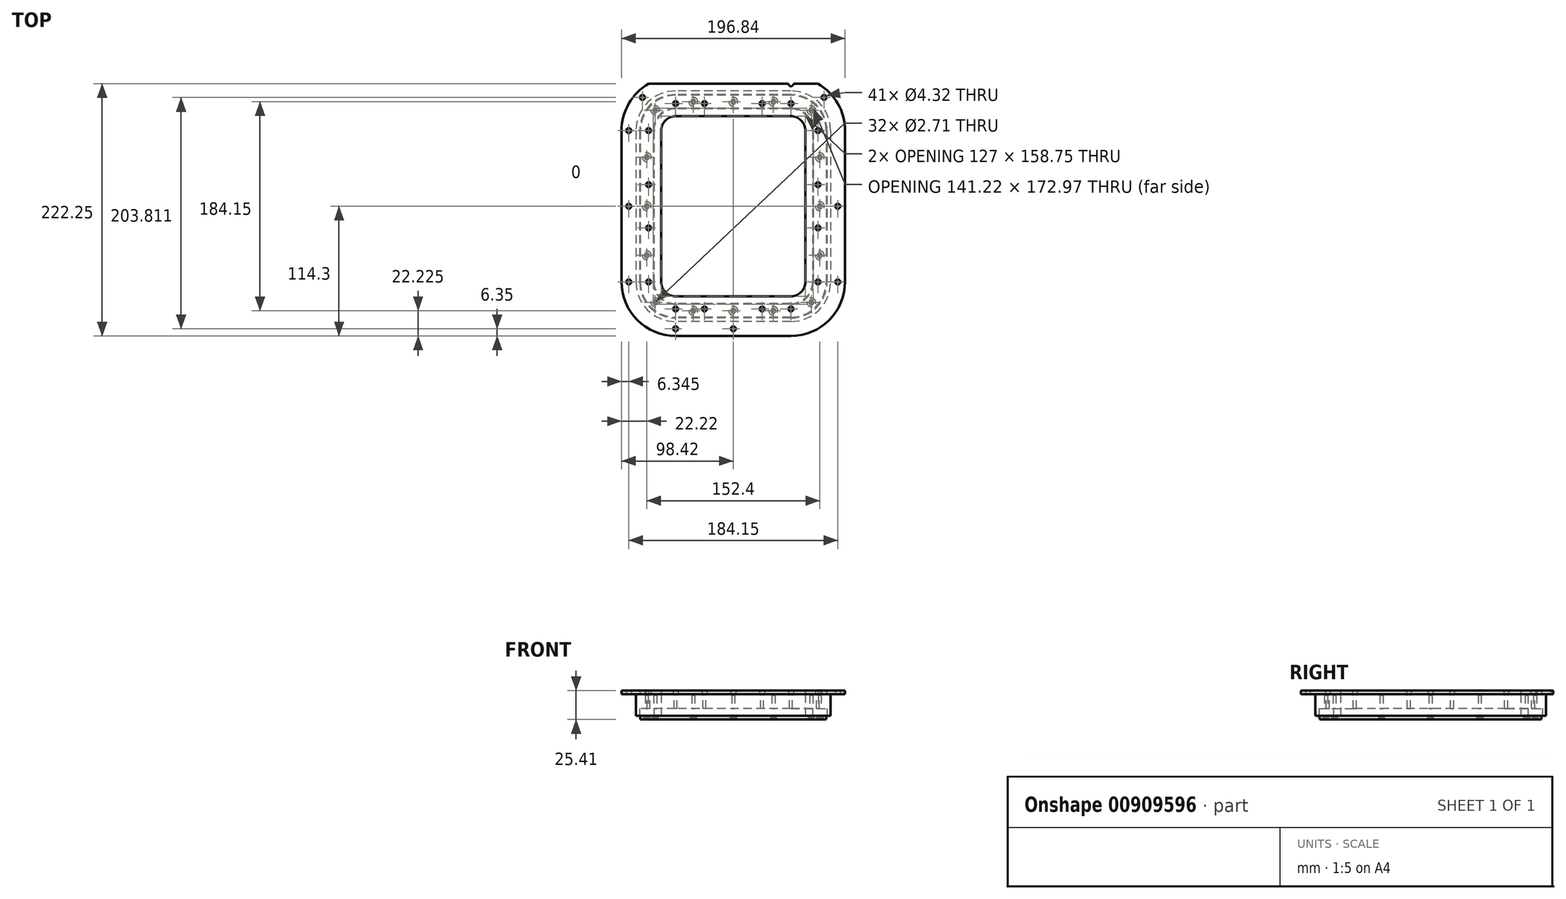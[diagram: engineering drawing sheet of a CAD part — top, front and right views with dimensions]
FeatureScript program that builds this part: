
annotation { "Feature Type Name" : "Feature", "Feature Type Description" : "" }
export const myFeature = defineFeature(function(context is Context, id is Id, definition is map)
    precondition{}
    {
        {
            var Q0;
            Q0=qCreatedBy(makeId("Top.planeOp"),FACE);
            var sketch = newSketch(context, id + "F0", { "sketchPlane" : qUnion([Q0])});
            skLineSegment(sketch, "E0.bottom", {"start": v(50.8, 79.38) * mm, "end": v(-50.8, 79.38) * mm});
            skLineSegment(sketch, "E0.top", {"start": v(50.8, -79.38) * mm, "end": v(-50.8, -79.38) * mm});
            skLineSegment(sketch, "E0.left", {"start": v(63.5, 66.67) * mm, "end": v(63.5, -66.67) * mm});
            skLineSegment(sketch, "E0.right", {"start": v(-63.5, 66.67) * mm, "end": v(-63.5, -66.67) * mm});
            skPoint(sketch, "E0.middle", {"position": v(0, 0) * mm});
            skPoint(sketch, "E1.visualSharp", {"position": v(-63.5, 79.38) * mm});
            skArc(sketch, "E1.filletArc", {"start": v(-50.8, 79.38) * mm, "mid": v(-59.78, 75.66) * mm, "end": v(-63.5, 66.67) * mm});
            skPoint(sketch, "E2.visualSharp", {"position": v(63.5, 79.38) * mm});
            skArc(sketch, "E2.filletArc", {"start": v(63.5, 66.67) * mm, "mid": v(59.78, 75.66) * mm, "end": v(50.8, 79.38) * mm});
            skPoint(sketch, "E3.visualSharp", {"position": v(63.5, -79.38) * mm});
            skArc(sketch, "E3.filletArc", {"start": v(50.8, -79.38) * mm, "mid": v(59.78, -75.66) * mm, "end": v(63.5, -66.67) * mm});
            skPoint(sketch, "E4.visualSharp", {"position": v(-63.5, -79.38) * mm});
            skArc(sketch, "E4.filletArc", {"start": v(-63.5, -66.67) * mm, "mid": v(-59.78, -75.66) * mm, "end": v(-50.8, -79.38) * mm});
            skArc(sketch, "E5.0", {"start": v(-50.8, 85.72) * mm, "mid": v(-64.27, 80.15) * mm, "end": v(-69.85, 66.67) * mm});
            skLineSegment(sketch, "E5.1", {"start": v(50.8, 85.72) * mm, "end": v(-50.8, 85.72) * mm});
            skLineSegment(sketch, "E5.2", {"start": v(-69.85, 66.67) * mm, "end": v(-69.85, -66.67) * mm});
            skArc(sketch, "E5.3", {"start": v(69.85, 66.67) * mm, "mid": v(64.27, 80.15) * mm, "end": v(50.8, 85.72) * mm});
            skArc(sketch, "E5.4", {"start": v(-69.85, -66.67) * mm, "mid": v(-64.27, -80.15) * mm, "end": v(-50.8, -85.72) * mm});
            skLineSegment(sketch, "E5.5", {"start": v(50.8, -85.72) * mm, "end": v(-50.8, -85.72) * mm});
            skArc(sketch, "E5.6", {"start": v(50.8, -85.72) * mm, "mid": v(64.27, -80.15) * mm, "end": v(69.85, -66.67) * mm});
            skLineSegment(sketch, "E5.7", {"start": v(69.85, 66.67) * mm, "end": v(69.85, -66.67) * mm});
            skLineSegment(sketch, "E6.0", {"start": v(-70.61, 66.67) * mm, "end": v(-70.61, -66.67) * mm});
            skArc(sketch, "E6.1", {"start": v(-50.8, 86.49) * mm, "mid": v(-64.8, 80.68) * mm, "end": v(-70.61, 66.67) * mm});
            skArc(sketch, "E6.2", {"start": v(-70.61, -66.67) * mm, "mid": v(-64.8, -80.68) * mm, "end": v(-50.8, -86.49) * mm});
            skLineSegment(sketch, "E6.3", {"start": v(50.8, 86.49) * mm, "end": v(-50.8, 86.49) * mm});
            skLineSegment(sketch, "E6.4", {"start": v(50.8, -86.49) * mm, "end": v(-50.8, -86.49) * mm});
            skArc(sketch, "E6.5", {"start": v(50.8, -86.49) * mm, "mid": v(64.8, -80.68) * mm, "end": v(70.61, -66.67) * mm});
            skLineSegment(sketch, "E6.6", {"start": v(70.61, 66.67) * mm, "end": v(70.61, -66.67) * mm});
            skArc(sketch, "E6.7", {"start": v(70.61, 66.67) * mm, "mid": v(64.8, 80.68) * mm, "end": v(50.8, 86.49) * mm});
            skArc(sketch, "E7.0", {"start": v(50.8, -98.42) * mm, "mid": v(73.25, -89.13) * mm, "end": v(82.55, -66.67) * mm});
            skLineSegment(sketch, "E7.1", {"start": v(82.55, 66.67) * mm, "end": v(82.55, -66.67) * mm});
            skLineSegment(sketch, "E7.2", {"start": v(50.8, -98.42) * mm, "end": v(-50.8, -98.42) * mm});
            skArc(sketch, "E7.3", {"start": v(82.55, 66.67) * mm, "mid": v(73.25, 89.13) * mm, "end": v(50.8, 98.42) * mm});
            skArc(sketch, "E7.4", {"start": v(-82.55, -66.67) * mm, "mid": v(-73.25, -89.13) * mm, "end": v(-50.8, -98.42) * mm});
            skLineSegment(sketch, "E7.5", {"start": v(-82.55, 66.67) * mm, "end": v(-82.55, -66.67) * mm});
            skArc(sketch, "E7.6", {"start": v(-50.8, 98.42) * mm, "mid": v(-73.25, 89.13) * mm, "end": v(-82.55, 66.67) * mm});
            skLineSegment(sketch, "E7.7", {"start": v(50.8, 98.42) * mm, "end": v(-50.8, 98.42) * mm});
            skArc(sketch, "E8.0", {"start": v(50.8, -101.6) * mm, "mid": v(75.5, -91.37) * mm, "end": v(85.72, -66.67) * mm});
            skLineSegment(sketch, "E8.1", {"start": v(85.73, 66.67) * mm, "end": v(85.73, -66.67) * mm});
            skLineSegment(sketch, "E8.2", {"start": v(50.8, -101.6) * mm, "end": v(-50.8, -101.6) * mm});
            skArc(sketch, "E8.3", {"start": v(85.73, 66.67) * mm, "mid": v(75.5, 91.37) * mm, "end": v(50.8, 101.6) * mm});
            skArc(sketch, "E8.4", {"start": v(-85.72, -66.67) * mm, "mid": v(-75.5, -91.37) * mm, "end": v(-50.8, -101.6) * mm});
            skLineSegment(sketch, "E8.5", {"start": v(-85.72, 66.67) * mm, "end": v(-85.72, -66.67) * mm});
            skArc(sketch, "E8.6", {"start": v(-50.8, 101.6) * mm, "mid": v(-75.5, 91.37) * mm, "end": v(-85.72, 66.67) * mm});
            skLineSegment(sketch, "E8.7", {"start": v(50.8, 101.6) * mm, "end": v(-50.8, 101.6) * mm});
            skArc(sketch, "E9.0", {"start": v(50.8, -97.66) * mm, "mid": v(72.71, -88.59) * mm, "end": v(81.79, -66.67) * mm});
            skLineSegment(sketch, "E9.1", {"start": v(81.79, 66.67) * mm, "end": v(81.79, -66.67) * mm});
            skLineSegment(sketch, "E9.2", {"start": v(50.8, -97.66) * mm, "end": v(-50.8, -97.66) * mm});
            skArc(sketch, "E9.3", {"start": v(81.79, 66.67) * mm, "mid": v(72.71, 88.59) * mm, "end": v(50.8, 97.66) * mm});
            skArc(sketch, "E9.4", {"start": v(-81.79, -66.67) * mm, "mid": v(-72.71, -88.59) * mm, "end": v(-50.8, -97.66) * mm});
            skLineSegment(sketch, "E9.5", {"start": v(-81.79, 66.67) * mm, "end": v(-81.79, -66.67) * mm});
            skArc(sketch, "E9.6", {"start": v(-50.8, 97.66) * mm, "mid": v(-72.71, 88.59) * mm, "end": v(-81.79, 66.67) * mm});
            skLineSegment(sketch, "E9.7", {"start": v(50.8, 97.66) * mm, "end": v(-50.8, 97.66) * mm});
            skSolve(sketch);
        }
        {
            var Q0;
            Q0=makeQuery(id+"F0.imprint","IMPRINT",FACE,{"disambiguationData":[TD([[makeQuery(id+"F0.imprint","IMPRINT",EDGE,{"derivedFrom":sQuery(id+"F0.wireOp",EDGE,"E0.bottom")}),-1.0]])]});
            var Q1;
            Q1=makeQuery(id+"F0.imprint","IMPRINT",FACE,{"disambiguationData":[TD([[makeQuery(id+"F0.imprint","IMPRINT",EDGE,{"derivedFrom":sQuery(id+"F0.wireOp",EDGE,"E6.0")}),-1.0]])]});
            var Q2;
            Q2=makeQuery(id+"F0.imprint","IMPRINT",FACE,{"disambiguationData":[TD([[makeQuery(id+"F0.imprint","IMPRINT",EDGE,{"derivedFrom":sQuery(id+"F0.wireOp",EDGE,"E7.0")}),1.0]])]});
            var Q3;
            Q3=makeQuery(id+"F0.imprint","IMPRINT",FACE,{"disambiguationData":[TD([[makeQuery(id+"F0.imprint","IMPRINT",EDGE,{"derivedFrom":sQuery(id+"F0.wireOp",EDGE,"E5.0")}),-1.0]])]});
            var Q4;
            Q4=makeQuery(id+"F0.imprint","IMPRINT",FACE,{"disambiguationData":[TD([[makeQuery(id+"F0.imprint","IMPRINT",EDGE,{"derivedFrom":sQuery(id+"F0.wireOp",EDGE,"E7.0")}),-1.0]])]});
            extrude(context, id + "F1", {"entities" : qUnion([Q0, Q1, Q2, Q3, Q4]), "depth" : 19.05 * mm, "offsetDistance" : 25.4 * mm});
        }
        {
            var Q0;
            Q0=makeQuery(id+"F0.imprint","IMPRINT",FACE,{"disambiguationData":[TD([[makeQuery(id+"F0.imprint","IMPRINT",EDGE,{"derivedFrom":sQuery(id+"F0.wireOp",EDGE,"E6.0")}),-1.0]])]});
            var Q1;
            Q1=makeQuery(id+"F0.imprint","IMPRINT",FACE,{"disambiguationData":[TD([[makeQuery(id+"F0.imprint","IMPRINT",EDGE,{"derivedFrom":sQuery(id+"F0.wireOp",EDGE,"E7.0")}),1.0]])]});
            var Q2;
            Q2=makeQuery(id+"F0.imprint","IMPRINT",FACE,{"disambiguationData":[TD([[makeQuery(id+"F0.imprint","IMPRINT",EDGE,{"derivedFrom":sQuery(id+"F0.wireOp",EDGE,"E5.0")}),-1.0]])]});
            extrude(context, id + "F2", {"entities" : qUnion([Q0, Q1, Q2]), "operationType" : NewBodyOperationType.REMOVE, "depth" : 6.35 * mm, "offsetDistance" : 25.4 * mm});
        }
        {
            var Q0;
            Q0=makeQuery(id+"F0.imprint","IMPRINT",FACE,{"disambiguationData":[TD([[makeQuery(id+"F0.imprint","IMPRINT",EDGE,{"derivedFrom":sQuery(id+"F0.wireOp",EDGE,"E6.0")}),-1.0]])]});
            extrude(context, id + "F3", {"entities" : qUnion([Q0]), "oppositeDirection" : true, "depth" : 3.17 * mm, "offsetDistance" : 25.4 * mm});
        }
        {
            var Q0;
            Q0=makeQuery(id+"F1.opExtrude","CAP_FACE",FACE,{"disambiguationData":[OSD([sQuery(id+"F0.wireOp",EDGE,"E0.bottom"),sQuery(id+"F0.wireOp",EDGE,"E0.top"),sQuery(id+"F0.wireOp",EDGE,"E0.left"),sQuery(id+"F0.wireOp",EDGE,"E0.right"),sQuery(id+"F0.wireOp",EDGE,"E1.filletArc"),sQuery(id+"F0.wireOp",EDGE,"E2.filletArc"),sQuery(id+"F0.wireOp",EDGE,"E3.filletArc"),sQuery(id+"F0.wireOp",EDGE,"E4.filletArc"),sQuery(id+"F0.wireOp",EDGE,"E8.0"),sQuery(id+"F0.wireOp",EDGE,"E8.1"),sQuery(id+"F0.wireOp",EDGE,"E8.2"),sQuery(id+"F0.wireOp",EDGE,"E8.3"),sQuery(id+"F0.wireOp",EDGE,"E8.4"),sQuery(id+"F0.wireOp",EDGE,"E8.5"),sQuery(id+"F0.wireOp",EDGE,"E8.6"),sQuery(id+"F0.wireOp",EDGE,"E8.7")])],"isStart":false});
            var sketch = newSketch(context, id + "F4", { "sketchPlane" : qUnion([Q0])});
            skLineSegment(sketch, "E10.bottom", {"start": v(50.8, 79.37) * mm, "end": v(-50.8, 79.38) * mm});
            skLineSegment(sketch, "E10.top", {"start": v(50.8, -79.38) * mm, "end": v(-50.8, -79.38) * mm});
            skLineSegment(sketch, "E10.left", {"start": v(63.5, 66.67) * mm, "end": v(63.5, -66.68) * mm});
            skLineSegment(sketch, "E10.right", {"start": v(-63.5, 66.67) * mm, "end": v(-63.5, -66.67) * mm});
            skPoint(sketch, "E10.middle", {"position": v(0, 0) * mm});
            skArc(sketch, "E11.filletArc", {"start": v(-50.8, 79.38) * mm, "mid": v(-59.78, 75.66) * mm, "end": v(-63.5, 66.67) * mm});
            skPoint(sketch, "E12.visualSharp", {"position": v(63.5, 79.38) * mm});
            skArc(sketch, "E12.filletArc", {"start": v(63.5, 66.67) * mm, "mid": v(59.78, 75.66) * mm, "end": v(50.8, 79.38) * mm});
            skPoint(sketch, "E13.visualSharp", {"position": v(63.5, -79.38) * mm});
            skArc(sketch, "E13.filletArc", {"start": v(50.8, -79.38) * mm, "mid": v(59.78, -75.66) * mm, "end": v(63.5, -66.68) * mm});
            skPoint(sketch, "E14.visualSharp", {"position": v(-63.5, -79.37) * mm});
            skArc(sketch, "E14.filletArc", {"start": v(-63.5, -66.67) * mm, "mid": v(-59.78, -75.66) * mm, "end": v(-50.8, -79.38) * mm});
            skArc(sketch, "E15.0", {"start": v(50.8, -114.3) * mm, "mid": v(84.48, -100.35) * mm, "end": v(98.42, -66.68) * mm});
            skLineSegment(sketch, "E15.1", {"start": v(98.43, 66.67) * mm, "end": v(98.42, -66.68) * mm});
            skLineSegment(sketch, "E15.2", {"start": v(50.8, -114.3) * mm, "end": v(-50.8, -114.3) * mm});
            skArc(sketch, "E15.3", {"start": v(98.43, 66.67) * mm, "mid": v(92.03, 90.51) * mm, "end": v(74.56, 107.95) * mm});
            skArc(sketch, "E15.4", {"start": v(-98.43, -66.67) * mm, "mid": v(-84.48, -100.35) * mm, "end": v(-50.8, -114.3) * mm});
            skLineSegment(sketch, "E15.5", {"start": v(-98.43, 66.68) * mm, "end": v(-98.43, -66.67) * mm});
            skArc(sketch, "E15.6", {"start": v(-74.56, 107.95) * mm, "mid": v(-92.03, 90.51) * mm, "end": v(-98.43, 66.68) * mm});
            skLineSegment(sketch, "E16.0", {"start": v(74.56, 107.95) * mm, "end": v(-74.56, 107.95) * mm});
            skArc(sketch, "E17.MirrorCS", {"start": v(63.5, -66.67) * mm, "mid": v(59.78, -75.66) * mm, "end": v(50.8, -79.38) * mm});
            skArc(sketch, "E18.MirrorCS", {"start": v(50.8, 79.38) * mm, "mid": v(59.78, 75.66) * mm, "end": v(63.5, 66.67) * mm});
            skLineSegment(sketch, "E19.MirrorCS", {"start": v(63.5, 66.67) * mm, "end": v(63.5, -66.67) * mm});
            skArc(sketch, "E20.MirrorCS", {"start": v(74.56, 107.95) * mm, "mid": v(92.03, 90.51) * mm, "end": v(98.43, 66.68) * mm});
            skLineSegment(sketch, "E21.MirrorCS", {"start": v(98.43, 66.68) * mm, "end": v(98.43, -66.67) * mm});
            skPoint(sketch, "E22.MirrorP", {"position": v(63.5, -79.37) * mm});
            skArc(sketch, "E23.MirrorCS", {"start": v(98.43, -66.67) * mm, "mid": v(84.48, -100.35) * mm, "end": v(50.8, -114.3) * mm});
            skArc(sketch, "E24.0", {"start": v(50.8, 107.95) * mm, "mid": v(79.99, 95.86) * mm, "end": v(92.08, 66.67) * mm, "construction": true});
            skLineSegment(sketch, "E24.1", {"start": v(92.08, 66.68) * mm, "end": v(92.08, -66.67) * mm, "construction": true});
            skLineSegment(sketch, "E24.2", {"start": v(50.8, 107.95) * mm, "end": v(-50.8, 107.95) * mm});
            skArc(sketch, "E24.3", {"start": v(92.08, -66.67) * mm, "mid": v(79.99, -95.86) * mm, "end": v(50.8, -107.95) * mm, "construction": true});
            skArc(sketch, "E24.4", {"start": v(-50.8, 107.95) * mm, "mid": v(-79.99, 95.86) * mm, "end": v(-92.08, 66.67) * mm, "construction": true});
            skLineSegment(sketch, "E24.5", {"start": v(-92.08, 66.68) * mm, "end": v(-92.08, -66.67) * mm, "construction": true});
            skArc(sketch, "E24.6", {"start": v(-92.08, -66.67) * mm, "mid": v(-79.99, -95.86) * mm, "end": v(-50.8, -107.95) * mm, "construction": true});
            skLineSegment(sketch, "E24.7", {"start": v(50.8, -107.95) * mm, "end": v(-50.8, -107.95) * mm, "construction": true});
            skCircle(sketch, "E25", {"center": v(-79.99, 95.86) * mm, "radius": 1.9 * mm, "construction": true});
            skCircle(sketch, "E26", {"center": v(0, -107.95) * mm, "radius": 1.9 * mm, "construction": true});
            skCircle(sketch, "E27", {"center": v(-50.8, -107.95) * mm, "radius": 1.9 * mm, "construction": true});
            skCircle(sketch, "E28", {"center": v(-92.08, -66.67) * mm, "radius": 1.9 * mm, "construction": true});
            skCircle(sketch, "E29", {"center": v(-92.08, 0) * mm, "radius": 1.9 * mm, "construction": true});
            skCircle(sketch, "E30", {"center": v(-92.08, 66.67) * mm, "radius": 1.9 * mm, "construction": true});
            skCircle(sketch, "E31", {"center": v(50.8, -107.95) * mm, "radius": 1.9 * mm, "construction": true});
            skCircle(sketch, "E32", {"center": v(92.08, -66.67) * mm, "radius": 1.9 * mm, "construction": true});
            skCircle(sketch, "E33", {"center": v(92.08, 0) * mm, "radius": 1.9 * mm, "construction": true});
            skCircle(sketch, "E34", {"center": v(92.08, 66.67) * mm, "radius": 1.9 * mm, "construction": true});
            skCircle(sketch, "E35", {"center": v(79.99, 95.86) * mm, "radius": 1.9 * mm, "construction": true});
            skSolve(sketch);
        }
        {
            var Q0;
            Q0=makeQuery(id+"F4.imprint","IMPRINT",FACE,{"disambiguationData":[TD([[makeQuery(id+"F4.imprint","IMPRINT",EDGE,{"derivedFrom":sQuery(id+"F4.wireOp",EDGE,"E15.0")}),1.0]])]});
            var Q1;
            Q1=makeQuery(id+"F4.imprint","IMPRINT",FACE,{"disambiguationData":[TD([[makeQuery(id+"F4.imprint","IMPRINT",EDGE,{"derivedFrom":sQuery(id+"F4.wireOp",EDGE,"E10.bottom")}),-1.0]])]});
            var Q2;
            Q2=makeQuery(id+"F4.imprint","IMPRINT",FACE,{"disambiguationData":[TD([[makeQuery(id+"F4.imprint","IMPRINT",EDGE,{"derivedFrom":sQuery(id+"F4.wireOp",EDGE,"E15.2")}),-1.0]])]});
            extrude(context, id + "F5", {"entities" : qUnion([Q0, Q1, Q2]), "depth" : 3.17 * mm, "offsetDistance" : 25.4 * mm});
        }
        {
            var Q0;
            Q0=makeQuery(id+"F3.opExtrude","CAP_FACE",FACE,{"disambiguationData":[OSD([sQuery(id+"F0.wireOp",EDGE,"E6.0"),sQuery(id+"F0.wireOp",EDGE,"E6.1"),sQuery(id+"F0.wireOp",EDGE,"E6.2"),sQuery(id+"F0.wireOp",EDGE,"E6.3"),sQuery(id+"F0.wireOp",EDGE,"E6.4"),sQuery(id+"F0.wireOp",EDGE,"E6.5"),sQuery(id+"F0.wireOp",EDGE,"E6.6"),sQuery(id+"F0.wireOp",EDGE,"E6.7"),sQuery(id+"F0.wireOp",EDGE,"E9.0"),sQuery(id+"F0.wireOp",EDGE,"E9.1"),sQuery(id+"F0.wireOp",EDGE,"E9.2"),sQuery(id+"F0.wireOp",EDGE,"E9.3"),sQuery(id+"F0.wireOp",EDGE,"E9.4"),sQuery(id+"F0.wireOp",EDGE,"E9.5"),sQuery(id+"F0.wireOp",EDGE,"E9.6"),sQuery(id+"F0.wireOp",EDGE,"E9.7")])],"isStart":false});
            var sketch = newSketch(context, id + "F6", { "sketchPlane" : qUnion([Q0])});
            skLineSegment(sketch, "E36", {"start": v(-64.8, 80.68) * mm, "end": v(-72.71, 88.59) * mm, "construction": true});
            skCircle(sketch, "E37", {"center": v(-68.76, 84.64) * mm, "radius": 1.9 * mm, "construction": true});
            skLineSegment(sketch, "E38", {"start": v(0, 97.66) * mm, "end": v(0, 0) * mm, "construction": true});
            skLineSegment(sketch, "E39", {"start": v(81.79, 0) * mm, "end": v(-81.79, 0) * mm, "construction": true});
            skPoint(sketch, "E40.orphan", {"position": v(0, -86.49) * mm});
            skCircle(sketch, "E41.MirrorC", {"center": v(68.76, 84.64) * mm, "radius": 1.9 * mm, "construction": true});
            skCircle(sketch, "E42.MirrorC", {"center": v(-68.76, -84.64) * mm, "radius": 1.9 * mm, "construction": true});
            skCircle(sketch, "E43.MirrorC", {"center": v(68.76, -84.64) * mm, "radius": 1.9 * mm, "construction": true});
            skCircle(sketch, "E44", {"center": v(0, 92.07) * mm, "radius": 1.9 * mm, "construction": true});
            skLineSegment(sketch, "E45", {"start": v(0, 97.66) * mm, "end": v(0, 86.49) * mm, "construction": true});
            skCircle(sketch, "E46", {"center": v(-35.3, 92.07) * mm, "radius": 1.9 * mm, "construction": true});
            skCircle(sketch, "E47.MirrorC", {"center": v(35.3, 92.07) * mm, "radius": 1.9 * mm, "construction": true});
            skCircle(sketch, "E48.MirrorC", {"center": v(-35.3, -92.07) * mm, "radius": 1.9 * mm, "construction": true});
            skCircle(sketch, "E49.MirrorC", {"center": v(35.3, -92.07) * mm, "radius": 1.9 * mm, "construction": true});
            skCircle(sketch, "E50.MirrorC", {"center": v(0, -92.07) * mm, "radius": 1.9 * mm, "construction": true});
            skLineSegment(sketch, "E51", {"start": v(-81.79, 0) * mm, "end": v(-70.61, 0) * mm, "construction": true});
            skCircle(sketch, "E52", {"center": v(-76.2, 0) * mm, "radius": 1.9 * mm, "construction": true});
            skCircle(sketch, "E53", {"center": v(-76.2, 43.24) * mm, "radius": 1.9 * mm, "construction": true});
            skCircle(sketch, "E54.MirrorC", {"center": v(-76.2, -43.24) * mm, "radius": 1.9 * mm, "construction": true});
            skCircle(sketch, "E55.MirrorC", {"center": v(76.2, 43.24) * mm, "radius": 1.9 * mm, "construction": true});
            skCircle(sketch, "E56.MirrorC", {"center": v(76.2, 0) * mm, "radius": 1.9 * mm, "construction": true});
            skCircle(sketch, "E57.MirrorC", {"center": v(76.2, -43.24) * mm, "radius": 1.9 * mm, "construction": true});
            skPoint(sketch, "E58", {"position": v(0, 0) * mm});
            skLineSegment(sketch, "E59", {"start": v(0, 0) * mm, "end": v(0, -97.66) * mm, "construction": true});
            skSolve(sketch);
        }
        {
            var Q0;
            Q0=sQuery(id+"F6.wireOp",VERTEX,"E37.center");
            var Q1;
            Q1=sQuery(id+"F6.wireOp",VERTEX,"E46.center");
            var Q2;
            Q2=sQuery(id+"F6.wireOp",VERTEX,"E44.center");
            var Q3;
            Q3=sQuery(id+"F6.wireOp",VERTEX,"E47.MirrorC.center");
            var Q4;
            Q4=sQuery(id+"F6.wireOp",VERTEX,"E41.MirrorC.center");
            var Q5;
            Q5=sQuery(id+"F6.wireOp",VERTEX,"E55.MirrorC.center");
            var Q6;
            Q6=sQuery(id+"F6.wireOp",VERTEX,"E56.MirrorC.center");
            var Q7;
            Q7=sQuery(id+"F6.wireOp",VERTEX,"E57.MirrorC.center");
            var Q8;
            Q8=sQuery(id+"F6.wireOp",VERTEX,"E43.MirrorC.center");
            var Q9;
            Q9=sQuery(id+"F6.wireOp",VERTEX,"E49.MirrorC.center");
            var Q10;
            Q10=sQuery(id+"F6.wireOp",VERTEX,"E50.MirrorC.center");
            var Q11;
            Q11=sQuery(id+"F6.wireOp",VERTEX,"E48.MirrorC.center");
            var Q12;
            Q12=sQuery(id+"F6.wireOp",VERTEX,"E42.MirrorC.center");
            var Q13;
            Q13=sQuery(id+"F6.wireOp",VERTEX,"E54.MirrorC.center");
            var Q14;
            Q14=sQuery(id+"F6.wireOp",VERTEX,"E52.center");
            var Q15;
            Q15=sQuery(id+"F6.wireOp",VERTEX,"E53.center");
            var Q16;
            Q16=makeQuery(id+"F3.opExtrude","SWEPT_BODY",BODY,{"disambiguationData":[OSD([sQuery(id+"F0.wireOp",EDGE,"E6.0"),sQuery(id+"F0.wireOp",EDGE,"E6.1"),sQuery(id+"F0.wireOp",EDGE,"E6.2"),sQuery(id+"F0.wireOp",EDGE,"E6.3"),sQuery(id+"F0.wireOp",EDGE,"E6.4"),sQuery(id+"F0.wireOp",EDGE,"E6.5"),sQuery(id+"F0.wireOp",EDGE,"E6.6"),sQuery(id+"F0.wireOp",EDGE,"E6.7"),sQuery(id+"F0.wireOp",EDGE,"E9.0"),sQuery(id+"F0.wireOp",EDGE,"E9.1"),sQuery(id+"F0.wireOp",EDGE,"E9.2"),sQuery(id+"F0.wireOp",EDGE,"E9.3"),sQuery(id+"F0.wireOp",EDGE,"E9.4"),sQuery(id+"F0.wireOp",EDGE,"E9.5"),sQuery(id+"F0.wireOp",EDGE,"E9.6"),sQuery(id+"F0.wireOp",EDGE,"E9.7")])]});
            hole(context, id + "F7", {"style" : HoleStyle.C_SINK, "endStyle" : HoleEndStyle.THROUGH, "standardTappedOrClearance" : lookupTablePath({ "fit" : "Normal (ASME)", "standard" : "ANSI", "size" : "#6", "type" : "Clearance" }), "standardBlindInLast" : lookupTablePath({ "fit" : "Normal", "standard" : "ANSI", "size" : "#6", "type" : "Clearance" }), "holeDiameter" : 4.32 * mm, "cSinkDiameter" : 7.8 * mm, "cSinkAngle" : 82 * degree, "majorDiameter" : 3.5 * mm, "isTappedThrough" : true, "tappedDepth" : 12.7 * mm, "tapClearance" : 3, "locations" : qUnion([Q0, Q1, Q2, Q3, Q4, Q5, Q6, Q7, Q8, Q9, Q10, Q11, Q12, Q13, Q14, Q15]), "scope" : qUnion([Q16])});
        }
        {
            var Q0;
            Q0=makeQuery(id+"F2.boolean.opBoolean","COPY",FACE,{"derivedFrom":makeQuery(id+"F2.opExtrude","CAP_FACE",FACE,{"disambiguationData":[OSD([sQuery(id+"F0.wireOp",EDGE,"E5.0"),sQuery(id+"F0.wireOp",EDGE,"E5.1"),sQuery(id+"F0.wireOp",EDGE,"E5.2"),sQuery(id+"F0.wireOp",EDGE,"E5.3"),sQuery(id+"F0.wireOp",EDGE,"E5.4"),sQuery(id+"F0.wireOp",EDGE,"E5.5"),sQuery(id+"F0.wireOp",EDGE,"E5.6"),sQuery(id+"F0.wireOp",EDGE,"E5.7"),sQuery(id+"F0.wireOp",EDGE,"E7.0"),sQuery(id+"F0.wireOp",EDGE,"E7.1"),sQuery(id+"F0.wireOp",EDGE,"E7.2"),sQuery(id+"F0.wireOp",EDGE,"E7.3"),sQuery(id+"F0.wireOp",EDGE,"E7.4"),sQuery(id+"F0.wireOp",EDGE,"E7.5"),sQuery(id+"F0.wireOp",EDGE,"E7.6"),sQuery(id+"F0.wireOp",EDGE,"E7.7")])],"isStart":false})});
            var sketch = newSketch(context, id + "F8", { "sketchPlane" : qUnion([Q0])});
            skLineSegment(sketch, "E60", {"start": v(-64.27, 80.15) * mm, "end": v(-73.25, 89.13) * mm, "construction": true});
            skCircle(sketch, "E61", {"center": v(-68.76, 84.64) * mm, "radius": 1.9 * mm, "construction": true});
            skLineSegment(sketch, "E62", {"start": v(0, 98.42) * mm, "end": v(0, 0) * mm, "construction": true});
            skLineSegment(sketch, "E63", {"start": v(82.55, 0) * mm, "end": v(-82.55, 0) * mm, "construction": true});
            skPoint(sketch, "E64.orphan", {"position": v(0, -85.72) * mm});
            skCircle(sketch, "E65.MirrorC", {"center": v(68.76, 84.64) * mm, "radius": 1.9 * mm, "construction": true});
            skCircle(sketch, "E66.MirrorC", {"center": v(-68.76, -84.64) * mm, "radius": 1.9 * mm, "construction": true});
            skCircle(sketch, "E67.MirrorC", {"center": v(68.76, -84.64) * mm, "radius": 1.9 * mm, "construction": true});
            skCircle(sketch, "E68", {"center": v(0, 92.08) * mm, "radius": 1.9 * mm, "construction": true});
            skLineSegment(sketch, "E69", {"start": v(0, 98.42) * mm, "end": v(0, 85.72) * mm, "construction": true});
            skCircle(sketch, "E70", {"center": v(-35.3, 92.08) * mm, "radius": 1.9 * mm, "construction": true});
            skCircle(sketch, "E71.MirrorC", {"center": v(35.3, 92.08) * mm, "radius": 1.9 * mm, "construction": true});
            skCircle(sketch, "E72.MirrorC", {"center": v(-35.3, -92.08) * mm, "radius": 1.9 * mm, "construction": true});
            skCircle(sketch, "E73.MirrorC", {"center": v(35.3, -92.08) * mm, "radius": 1.9 * mm, "construction": true});
            skCircle(sketch, "E74.MirrorC", {"center": v(0, -92.08) * mm, "radius": 1.9 * mm, "construction": true});
            skLineSegment(sketch, "E75", {"start": v(-82.55, 0) * mm, "end": v(-69.85, 0) * mm, "construction": true});
            skCircle(sketch, "E76", {"center": v(-76.2, 0) * mm, "radius": 1.9 * mm, "construction": true});
            skCircle(sketch, "E77", {"center": v(-76.2, 43.24) * mm, "radius": 1.9 * mm, "construction": true});
            skCircle(sketch, "E78.MirrorC", {"center": v(-76.2, -43.24) * mm, "radius": 1.9 * mm, "construction": true});
            skCircle(sketch, "E79.MirrorC", {"center": v(76.2, 43.24) * mm, "radius": 1.9 * mm, "construction": true});
            skCircle(sketch, "E80.MirrorC", {"center": v(76.2, 0) * mm, "radius": 1.9 * mm, "construction": true});
            skCircle(sketch, "E81.MirrorC", {"center": v(76.2, -43.24) * mm, "radius": 1.9 * mm, "construction": true});
            skPoint(sketch, "E82", {"position": v(0, 0) * mm});
            skLineSegment(sketch, "E83", {"start": v(0, 0) * mm, "end": v(0, -98.42) * mm, "construction": true});
            skSolve(sketch);
        }
        {
            var Q0;
            Q0=sQuery(id+"F8.wireOp",VERTEX,"E61.center");
            var Q1;
            Q1=sQuery(id+"F8.wireOp",VERTEX,"E70.center");
            var Q2;
            Q2=sQuery(id+"F8.wireOp",VERTEX,"E68.center");
            var Q3;
            Q3=sQuery(id+"F8.wireOp",VERTEX,"E71.MirrorC.center");
            var Q4;
            Q4=sQuery(id+"F8.wireOp",VERTEX,"E65.MirrorC.center");
            var Q5;
            Q5=sQuery(id+"F8.wireOp",VERTEX,"E79.MirrorC.center");
            var Q6;
            Q6=sQuery(id+"F8.wireOp",VERTEX,"E80.MirrorC.center");
            var Q7;
            Q7=sQuery(id+"F8.wireOp",VERTEX,"E81.MirrorC.center");
            var Q8;
            Q8=sQuery(id+"F8.wireOp",VERTEX,"E67.MirrorC.center");
            var Q9;
            Q9=sQuery(id+"F8.wireOp",VERTEX,"E73.MirrorC.center");
            var Q10;
            Q10=sQuery(id+"F8.wireOp",VERTEX,"E74.MirrorC.center");
            var Q11;
            Q11=sQuery(id+"F8.wireOp",VERTEX,"E72.MirrorC.center");
            var Q12;
            Q12=sQuery(id+"F8.wireOp",VERTEX,"E66.MirrorC.center");
            var Q13;
            Q13=sQuery(id+"F8.wireOp",VERTEX,"E78.MirrorC.center");
            var Q14;
            Q14=sQuery(id+"F8.wireOp",VERTEX,"E76.center");
            var Q15;
            Q15=sQuery(id+"F8.wireOp",VERTEX,"E77.center");
            var Q16;
            Q16=makeQuery(id+"F1.opExtrude","SWEPT_BODY",BODY,{"disambiguationData":[OSD([sQuery(id+"F0.wireOp",EDGE,"E0.bottom"),sQuery(id+"F0.wireOp",EDGE,"E0.top"),sQuery(id+"F0.wireOp",EDGE,"E0.left"),sQuery(id+"F0.wireOp",EDGE,"E0.right"),sQuery(id+"F0.wireOp",EDGE,"E1.filletArc"),sQuery(id+"F0.wireOp",EDGE,"E2.filletArc"),sQuery(id+"F0.wireOp",EDGE,"E3.filletArc"),sQuery(id+"F0.wireOp",EDGE,"E4.filletArc"),sQuery(id+"F0.wireOp",EDGE,"E8.0"),sQuery(id+"F0.wireOp",EDGE,"E8.1"),sQuery(id+"F0.wireOp",EDGE,"E8.2"),sQuery(id+"F0.wireOp",EDGE,"E8.3"),sQuery(id+"F0.wireOp",EDGE,"E8.4"),sQuery(id+"F0.wireOp",EDGE,"E8.5"),sQuery(id+"F0.wireOp",EDGE,"E8.6"),sQuery(id+"F0.wireOp",EDGE,"E8.7")])]});
            hole(context, id + "F9", {"style" : HoleStyle.SIMPLE, "endStyle" : HoleEndStyle.BLIND, "standardTappedOrClearance" : lookupTablePath({ "standard" : "ANSI", "engagement" : "75%", "pitch" : "32 tpi", "size" : "#6", "type" : "Tapped" }), "standardBlindInLast" : lookupTablePath({ "standard" : "ANSI", "engagement" : "75%", "pitch" : "32 tpi", "size" : "#6", "type" : "Tapped" }), "holeDiameter" : 2.7 * mm, "majorDiameter" : 3.5 * mm, "showTappedDepth" : true, "holeDepth" : 11.9 * mm, "isTappedThrough" : true, "tappedDepth" : 9.52 * mm, "tapClearance" : 3, "locations" : qUnion([Q0, Q1, Q2, Q3, Q4, Q5, Q6, Q7, Q8, Q9, Q10, Q11, Q12, Q13, Q14, Q15]), "scope" : qUnion([Q16])});
        }
        {
            var Q0;
            Q0=makeQuery(id+"F1.opExtrude","CAP_FACE",FACE,{"disambiguationData":[OSD([sQuery(id+"F0.wireOp",EDGE,"E0.bottom"),sQuery(id+"F0.wireOp",EDGE,"E0.top"),sQuery(id+"F0.wireOp",EDGE,"E0.left"),sQuery(id+"F0.wireOp",EDGE,"E0.right"),sQuery(id+"F0.wireOp",EDGE,"E1.filletArc"),sQuery(id+"F0.wireOp",EDGE,"E2.filletArc"),sQuery(id+"F0.wireOp",EDGE,"E3.filletArc"),sQuery(id+"F0.wireOp",EDGE,"E4.filletArc"),sQuery(id+"F0.wireOp",EDGE,"E8.0"),sQuery(id+"F0.wireOp",EDGE,"E8.1"),sQuery(id+"F0.wireOp",EDGE,"E8.2"),sQuery(id+"F0.wireOp",EDGE,"E8.3"),sQuery(id+"F0.wireOp",EDGE,"E8.4"),sQuery(id+"F0.wireOp",EDGE,"E8.5"),sQuery(id+"F0.wireOp",EDGE,"E8.6"),sQuery(id+"F0.wireOp",EDGE,"E8.7")])],"isStart":false});
            var sketch = newSketch(context, id + "F10", { "sketchPlane" : qUnion([Q0])});
            skLineSegment(sketch, "E84", {"start": v(0, 101.6) * mm, "end": v(0, 79.38) * mm, "construction": true});
            skLineSegment(sketch, "E85", {"start": v(-85.72, 0) * mm, "end": v(-63.5, 0) * mm, "construction": true});
            skCircle(sketch, "E86", {"center": v(-50.8, 90.49) * mm, "radius": 1.9 * mm, "construction": true});
            skPoint(sketch, "E86.centerSnap0", {"position": v(0, 90.49) * mm});
            skCircle(sketch, "E87.MirrorC", {"center": v(50.8, 90.49) * mm, "radius": 1.9 * mm, "construction": true});
            skCircle(sketch, "E88", {"center": v(-25.4, 90.49) * mm, "radius": 1.9 * mm});
            skCircle(sketch, "E89.MirrorC", {"center": v(25.4, 90.49) * mm, "radius": 1.9 * mm});
            skCircle(sketch, "E90", {"center": v(-74.61, 66.68) * mm, "radius": 1.9 * mm});
            skPoint(sketch, "E90.centerSnap0", {"position": v(-74.61, 0) * mm});
            skCircle(sketch, "E91", {"center": v(-74.61, 19.05) * mm, "radius": 1.9 * mm});
            skCircle(sketch, "E92.MirrorC", {"center": v(-74.61, -19.05) * mm, "radius": 1.9 * mm});
            skCircle(sketch, "E93.MirrorC", {"center": v(-74.61, -66.68) * mm, "radius": 1.9 * mm});
            skCircle(sketch, "E94.MirrorC", {"center": v(-50.8, -90.49) * mm, "radius": 1.9 * mm, "construction": true});
            skCircle(sketch, "E95.MirrorC", {"center": v(-25.4, -90.49) * mm, "radius": 1.9 * mm});
            skCircle(sketch, "E96.MirrorC", {"center": v(25.4, -90.49) * mm, "radius": 1.9 * mm});
            skCircle(sketch, "E97.MirrorC", {"center": v(50.8, -90.49) * mm, "radius": 1.9 * mm, "construction": true});
            skCircle(sketch, "E98.MirrorC", {"center": v(74.61, 19.05) * mm, "radius": 1.9 * mm});
            skCircle(sketch, "E99.MirrorC", {"center": v(74.61, 66.68) * mm, "radius": 1.9 * mm});
            skCircle(sketch, "E100.MirrorC", {"center": v(74.61, -66.68) * mm, "radius": 1.9 * mm});
            skCircle(sketch, "E101.MirrorC", {"center": v(74.61, -19.05) * mm, "radius": 1.9 * mm});
            skLineSegment(sketch, "E102.MirrorCS", {"start": v(85.72, 0) * mm, "end": v(63.5, 0) * mm, "construction": true});
            skPoint(sketch, "E103.MirrorP", {"position": v(74.61, 0) * mm});
            skSolve(sketch);
        }
        {
            var Q0;
            Q0=sQuery(id+"F10.wireOp",VERTEX,"E90.center");
            var Q1;
            Q1=sQuery(id+"F10.wireOp",VERTEX,"E86.center");
            var Q2;
            Q2=sQuery(id+"F10.wireOp",VERTEX,"E88.center");
            var Q3;
            Q3=sQuery(id+"F10.wireOp",VERTEX,"E89.MirrorC.center");
            var Q4;
            Q4=sQuery(id+"F10.wireOp",VERTEX,"E87.MirrorC.center");
            var Q5;
            Q5=sQuery(id+"F10.wireOp",VERTEX,"E99.MirrorC.center");
            var Q6;
            Q6=sQuery(id+"F10.wireOp",VERTEX,"E98.MirrorC.center");
            var Q7;
            Q7=sQuery(id+"F10.wireOp",VERTEX,"E101.MirrorC.center");
            var Q8;
            Q8=sQuery(id+"F10.wireOp",VERTEX,"E100.MirrorC.center");
            var Q9;
            Q9=sQuery(id+"F10.wireOp",VERTEX,"E97.MirrorC.center");
            var Q10;
            Q10=sQuery(id+"F10.wireOp",VERTEX,"E96.MirrorC.center");
            var Q11;
            Q11=sQuery(id+"F10.wireOp",VERTEX,"E95.MirrorC.center");
            var Q12;
            Q12=sQuery(id+"F10.wireOp",VERTEX,"E94.MirrorC.center");
            var Q13;
            Q13=sQuery(id+"F10.wireOp",VERTEX,"E93.MirrorC.center");
            var Q14;
            Q14=sQuery(id+"F10.wireOp",VERTEX,"E92.MirrorC.center");
            var Q15;
            Q15=sQuery(id+"F10.wireOp",VERTEX,"E91.center");
            var Q16;
            Q16=makeQuery(id+"F1.opExtrude","SWEPT_BODY",BODY,{"disambiguationData":[OSD([sQuery(id+"F0.wireOp",EDGE,"E0.bottom"),sQuery(id+"F0.wireOp",EDGE,"E0.top"),sQuery(id+"F0.wireOp",EDGE,"E0.left"),sQuery(id+"F0.wireOp",EDGE,"E0.right"),sQuery(id+"F0.wireOp",EDGE,"E1.filletArc"),sQuery(id+"F0.wireOp",EDGE,"E2.filletArc"),sQuery(id+"F0.wireOp",EDGE,"E3.filletArc"),sQuery(id+"F0.wireOp",EDGE,"E4.filletArc"),sQuery(id+"F0.wireOp",EDGE,"E8.0"),sQuery(id+"F0.wireOp",EDGE,"E8.1"),sQuery(id+"F0.wireOp",EDGE,"E8.2"),sQuery(id+"F0.wireOp",EDGE,"E8.3"),sQuery(id+"F0.wireOp",EDGE,"E8.4"),sQuery(id+"F0.wireOp",EDGE,"E8.5"),sQuery(id+"F0.wireOp",EDGE,"E8.6"),sQuery(id+"F0.wireOp",EDGE,"E8.7")])]});
            hole(context, id + "F11", {"style" : HoleStyle.SIMPLE, "endStyle" : HoleEndStyle.BLIND, "standardTappedOrClearance" : lookupTablePath({ "standard" : "ANSI", "engagement" : "75%", "pitch" : "32 tpi", "size" : "#6", "type" : "Tapped" }), "standardBlindInLast" : lookupTablePath({ "standard" : "ANSI", "engagement" : "75%", "pitch" : "32 tpi", "size" : "#6", "type" : "Tapped" }), "holeDiameter" : 2.7 * mm, "majorDiameter" : 3.5 * mm, "showTappedDepth" : true, "holeDepth" : 12.7 * mm, "isTappedThrough" : true, "tappedDepth" : 10.32 * mm, "tapClearance" : 3, "locations" : qUnion([Q0, Q1, Q2, Q3, Q4, Q5, Q6, Q7, Q8, Q9, Q10, Q11, Q12, Q13, Q14, Q15]), "scope" : qUnion([Q16])});
        }
        {
            var Q0;
            Q0=sQuery(id+"F10.wireOp",VERTEX,"E91.center");
            var Q1;
            Q1=sQuery(id+"F10.wireOp",VERTEX,"E90.center");
            var Q2;
            Q2=sQuery(id+"F10.wireOp",VERTEX,"E86.center");
            var Q3;
            Q3=sQuery(id+"F10.wireOp",VERTEX,"E88.center");
            var Q4;
            Q4=sQuery(id+"F10.wireOp",VERTEX,"E89.MirrorC.center");
            var Q5;
            Q5=sQuery(id+"F10.wireOp",VERTEX,"E87.MirrorC.center");
            var Q6;
            Q6=sQuery(id+"F10.wireOp",VERTEX,"E99.MirrorC.center");
            var Q7;
            Q7=sQuery(id+"F10.wireOp",VERTEX,"E98.MirrorC.center");
            var Q8;
            Q8=sQuery(id+"F10.wireOp",VERTEX,"E101.MirrorC.center");
            var Q9;
            Q9=sQuery(id+"F10.wireOp",VERTEX,"E92.MirrorC.center");
            var Q10;
            Q10=sQuery(id+"F10.wireOp",VERTEX,"E93.MirrorC.center");
            var Q11;
            Q11=sQuery(id+"F10.wireOp",VERTEX,"E94.MirrorC.center");
            var Q12;
            Q12=sQuery(id+"F10.wireOp",VERTEX,"E95.MirrorC.center");
            var Q13;
            Q13=sQuery(id+"F10.wireOp",VERTEX,"E96.MirrorC.center");
            var Q14;
            Q14=sQuery(id+"F10.wireOp",VERTEX,"E97.MirrorC.center");
            var Q15;
            Q15=sQuery(id+"F10.wireOp",VERTEX,"E100.MirrorC.center");
            var Q16;
            Q16=makeQuery(id+"F5.opExtrude","SWEPT_BODY",BODY,{"disambiguationData":[OSD([sQuery(id+"F4.wireOp",EDGE,"E10.bottom"),sQuery(id+"F4.wireOp",EDGE,"E10.top"),sQuery(id+"F4.wireOp",EDGE,"E10.left"),sQuery(id+"F4.wireOp",EDGE,"E10.right"),sQuery(id+"F4.wireOp",EDGE,"E11.filletArc"),sQuery(id+"F4.wireOp",EDGE,"E12.filletArc"),sQuery(id+"F4.wireOp",EDGE,"E13.filletArc"),sQuery(id+"F4.wireOp",EDGE,"E14.filletArc"),sQuery(id+"F4.wireOp",EDGE,"E15.0"),sQuery(id+"F4.wireOp",EDGE,"E15.1"),sQuery(id+"F4.wireOp",EDGE,"E15.2"),sQuery(id+"F4.wireOp",EDGE,"E15.3"),sQuery(id+"F4.wireOp",EDGE,"E15.4"),sQuery(id+"F4.wireOp",EDGE,"E15.5"),sQuery(id+"F4.wireOp",EDGE,"E15.6"),sQuery(id+"F4.wireOp",EDGE,"E16.0")])]});
            hole(context, id + "F12", {"style" : HoleStyle.SIMPLE, "endStyle" : HoleEndStyle.THROUGH, "oppositeDirection" : true, "standardTappedOrClearance" : lookupTablePath({ "fit" : "Normal (ASME)", "standard" : "ANSI", "size" : "#6", "type" : "Clearance" }), "standardBlindInLast" : lookupTablePath({ "fit" : "Normal", "standard" : "ANSI", "size" : "#6", "type" : "Clearance" }), "holeDiameter" : 4.32 * mm, "majorDiameter" : 3.5 * mm, "isTappedThrough" : true, "tappedDepth" : 10.32 * mm, "tapClearance" : 3, "locations" : qUnion([Q0, Q1, Q2, Q3, Q4, Q5, Q6, Q7, Q8, Q9, Q10, Q11, Q12, Q13, Q14, Q15]), "scope" : qUnion([Q16])});
        }
        {
            var Q0;
            Q0=sQuery(id+"F4.wireOp",VERTEX,"E24.4.end");
            var Q1;
            Q1=sQuery(id+"F4.wireOp",VERTEX,"E25.center");
            var Q2;
            Q2=sQuery(id+"F4.wireOp",VERTEX,"E35.center");
            var Q3;
            Q3=sQuery(id+"F4.wireOp",VERTEX,"E24.0.end");
            var Q4;
            Q4=sQuery(id+"F4.wireOp",VERTEX,"E33.center");
            var Q5;
            Q5=sQuery(id+"F4.wireOp",VERTEX,"E24.1.end");
            var Q6;
            Q6=sQuery(id+"F4.wireOp",VERTEX,"E24.3.end");
            var Q7;
            Q7=sQuery(id+"F4.wireOp",VERTEX,"E26.center");
            var Q8;
            Q8=sQuery(id+"F4.wireOp",VERTEX,"E24.6.end");
            var Q9;
            Q9=sQuery(id+"F4.wireOp",VERTEX,"E24.5.end");
            var Q10;
            Q10=sQuery(id+"F4.wireOp",VERTEX,"E29.center");
            var Q11;
            Q11=makeQuery(id+"F5.opExtrude","SWEPT_BODY",BODY,{"disambiguationData":[OSD([sQuery(id+"F4.wireOp",EDGE,"E10.bottom"),sQuery(id+"F4.wireOp",EDGE,"E10.top"),sQuery(id+"F4.wireOp",EDGE,"E10.right"),sQuery(id+"F4.wireOp",EDGE,"E11.filletArc"),sQuery(id+"F4.wireOp",EDGE,"E14.filletArc"),sQuery(id+"F4.wireOp",EDGE,"E15.2"),sQuery(id+"F4.wireOp",EDGE,"E15.4"),sQuery(id+"F4.wireOp",EDGE,"E15.5"),sQuery(id+"F4.wireOp",EDGE,"E15.6"),sQuery(id+"F4.wireOp",EDGE,"E16.0"),sQuery(id+"F4.wireOp",EDGE,"E17.MirrorCS"),sQuery(id+"F4.wireOp",EDGE,"E18.MirrorCS"),sQuery(id+"F4.wireOp",EDGE,"E19.MirrorCS"),sQuery(id+"F4.wireOp",EDGE,"E20.MirrorCS"),sQuery(id+"F4.wireOp",EDGE,"E21.MirrorCS"),sQuery(id+"F4.wireOp",EDGE,"E23.MirrorCS")])]});
            hole(context, id + "F13", {"style" : HoleStyle.SIMPLE, "endStyle" : HoleEndStyle.THROUGH, "oppositeDirection" : true, "standardTappedOrClearance" : lookupTablePath({ "fit" : "Normal (ASME)", "standard" : "ANSI", "size" : "#6", "type" : "Clearance" }), "standardBlindInLast" : lookupTablePath({ "fit" : "Normal", "standard" : "ANSI", "size" : "#6", "type" : "Clearance" }), "holeDiameter" : 4.32 * mm, "majorDiameter" : 6.35 * mm, "isTappedThrough" : true, "tappedDepth" : 10.3 * mm, "tapClearance" : 3, "locations" : qUnion([Q0, Q1, Q2, Q3, Q4, Q5, Q6, Q7, Q8, Q9, Q10]), "scope" : qUnion([Q11])});
        }
    });
